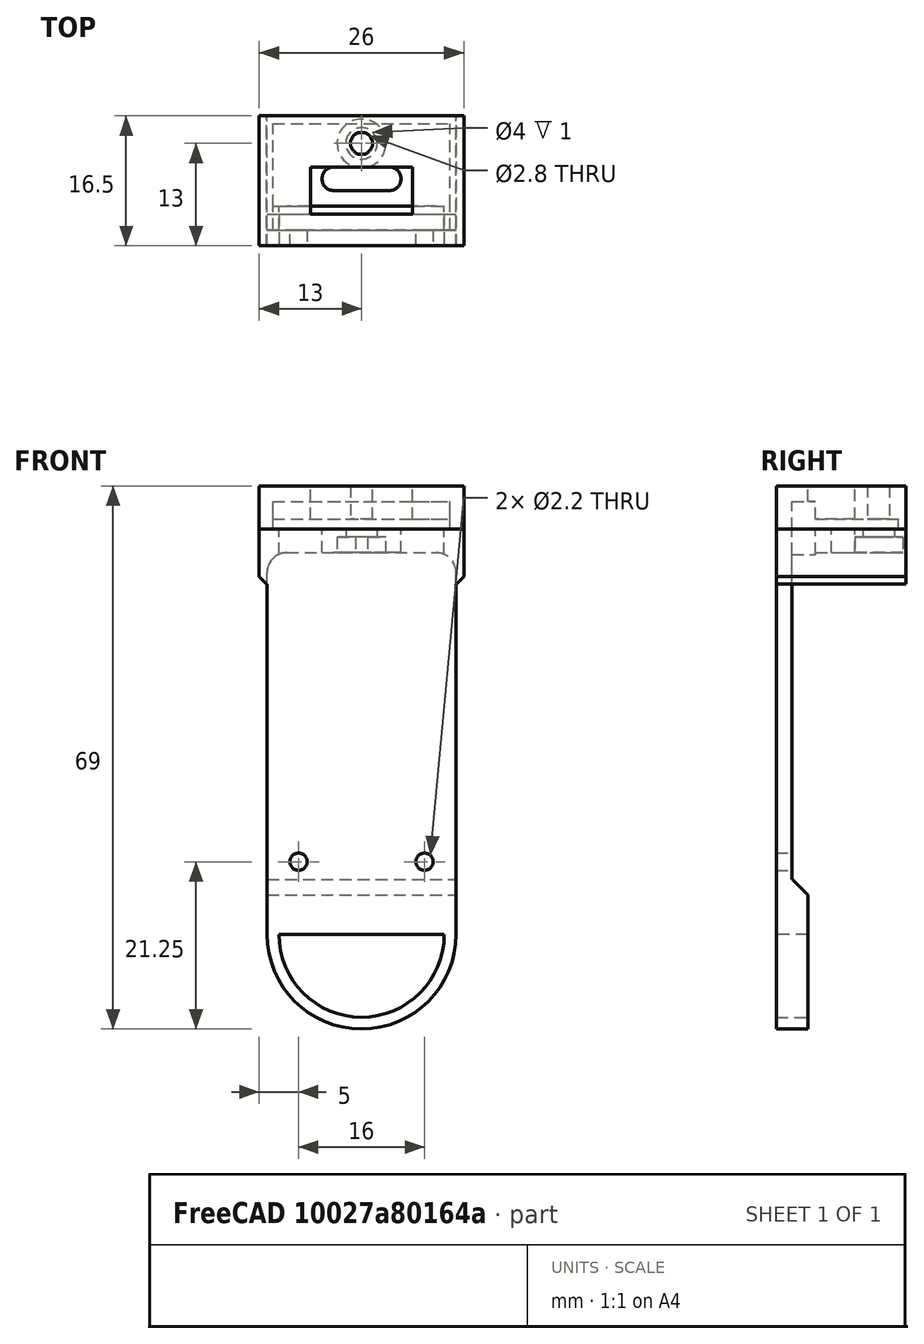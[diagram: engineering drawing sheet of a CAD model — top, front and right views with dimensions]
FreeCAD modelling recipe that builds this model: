
FCSTD DOCUMENT  (FreeCAD 1.0R39319 (Git))
Label: m5_stick_dht11
License: All rights reserved
LicenseURL: http://en.wikipedia.org/wiki/All_rights_reserved
objects: Part::Box×10, Part::Cylinder×7, Part::Cut×6, Part::MultiFuse×5, Part::Fillet×2, Part::Chamfer×2
note: 32 computed .brp shape members not serialized (recipe doc carries the construction recipe); baked Part::Feature solids carry a one-line shape summary decoded from their .brp

FEATURE [Part::Box] Box  label="Cube(inner_base)"
  AttacherType = Attacher::AttachEngine3D
  Height = 4
  Length = 24
  Width = 14.5
FEATURE [Part::Box] Box001  label="Cube(outer_base)"
  AttacherType = Attacher::AttachEngine3D
  Height = 7
  Length = 26
  Placement = pos=(-1,-2,0) rot=(0,0,1;0rad)
  Width = 16.5
FEATURE [Part::Fillet] Fillet
  Base = -> Box
  EdgeLinks = -> Box [Edge2,Edge6]
  Edges = 2 edges r=2.5: [Edge2,Edge6]
FEATURE [Part::Box] Box002  label="Cube(header_cutter)"
  AttacherType = Attacher::AttachEngine3D
  Height = 7
  Length = 21
  Placement = pos=(1.5,0,0) rot=(0,0,1;0rad)
  Width = 3
FEATURE [Part::Box] Box003  label="Cube(ir_reciever_header_cutter)"
  AttacherType = Attacher::AttachEngine3D
  Height = 7
  Length = 10
  Placement = pos=(7,5,0) rot=(0,0,1;0rad)
  Width = 3
FEATURE [Part::Fillet] Fillet001
  Base = -> Box003
  EdgeLinks = -> Box003 [Edge1,Edge3,Edge5,Edge7]
  Edges = 4 edges r=1.45: [Edge1,Edge3,Edge5,Edge7]
FEATURE [Part::Box] Box004  label="Cube(pcb_cut)"
  AttacherType = Attacher::AttachEngine3D
  Height = 3.5
  Length = 22.5
  Placement = pos=(0.75,0,7) rot=(0,0,1;0rad)
  Width = 3
FEATURE [Part::Box] Box005  label="Cube(top_cover)"
  AttacherType = Attacher::AttachEngine3D
  Height = 5.5
  Length = 26
  Placement = pos=(-1,-2,7) rot=(0,0,1;0rad)
  Width = 16.5
FEATURE [Part::Box] Box007  label="Cube(back_cover)"
  AttacherType = Attacher::AttachEngine3D
  Height = 43.5
  Length = 24
  Placement = pos=(0,-2,-37.5) rot=(0,0,1;0rad)
  Width = 2
FEATURE [Part::Cylinder] Cylinder001  label="Cylinder001(right_bolt_clear)"
  Angle = 360
  AttacherType = Attacher::AttachEngine3D
  FirstAngle = 0
  Height = 10
  Placement = pos=(4,0,-35.25) rot=(1,0,0;1.5708rad)
  Radius = 1.1
  SecondAngle = 0
FEATURE [Part::Cylinder] Cylinder002  label="Cylinder002(left_bolt_clear)"
  Angle = 360
  AttacherType = Attacher::AttachEngine3D
  FirstAngle = 0
  Height = 10
  Placement = pos=(20,0,-35.25) rot=(1,0,0;1.5708rad)
  Radius = 1.1
  SecondAngle = 0
FEATURE [Part::MultiFuse] Fusion004
  Shapes = -> [Cylinder002,Cylinder001]
FEATURE [Part::Cylinder] Cylinder005  label="Cylinder005(bolt_head)"
  Angle = 360
  AttacherType = Attacher::AttachEngine3D
  FirstAngle = 0
  Height = 2
  Placement = pos=(12,11,4) rot=(0,0,1;0rad)
  Radius = 3.1
  SecondAngle = 0
FEATURE [Part::Cut] Cut
  Base = -> Box001
  Tool = -> Fillet
FEATURE [Part::Cylinder] Cylinder006  label="Cylinder005(bolt_clear)"
  Angle = 360
  AttacherType = Attacher::AttachEngine3D
  FirstAngle = 0
  Height = 2
  Placement = pos=(12,11,5) rot=(0,0,1;0rad)
  Radius = 2
  SecondAngle = 0
FEATURE [Part::MultiFuse] Fusion
  Shapes = -> [Cylinder006,Cylinder005,Box002,Fillet001]
FEATURE [Part::Cut] Cut001
  Base = -> Cut
  Tool = -> Fusion
FEATURE [Part::Cylinder] Cylinder007  label="Cylinder005(bolt_thread)"
  Angle = 360
  AttacherType = Attacher::AttachEngine3D
  FirstAngle = 0
  Height = 6
  Placement = pos=(12,11,7) rot=(0,0,1;0rad)
  Radius = 1.4
  SecondAngle = 0
FEATURE [Part::Box] Box010  label="Cube(dht11)"
  AttacherType = Attacher::AttachEngine3D
  Height = 10
  Length = 13
  Placement = pos=(5.5,2,7) rot=(0,0,1;0rad)
  Width = 6
FEATURE [Part::MultiFuse] Fusion007
  Shapes = -> [Box010,Cylinder007,Box004]
FEATURE [Part::Cut] Cut003
  Base = -> Box005
  Tool = -> Fusion007
FEATURE [Part::Box] Box011  label="Cube(back_rest)"
  AttacherType = Attacher::AttachEngine3D
  Height = 7
  Length = 24
  Placement = pos=(0,-2,-44.5) rot=(0,0,1;0rad)
  Width = 4
FEATURE [Part::Cylinder] Cylinder008  label="Cylinder008(outer_hook)"
  Angle = 180
  AttacherType = Attacher::AttachEngine3D
  FirstAngle = 0
  Height = 4
  Placement = pos=(12,2,-44.5) rot=(0,0.707107,-0.707107;3.14159rad)
  Radius = 12
  SecondAngle = 0
FEATURE [Part::Cylinder] Cylinder009  label="Cylinder008(inner_hook)"
  Angle = 180
  AttacherType = Attacher::AttachEngine3D
  FirstAngle = 0
  Height = 4
  Placement = pos=(12,2,-44.5) rot=(0,0.707107,-0.707107;3.14159rad)
  Radius = 10.5
  SecondAngle = 0
FEATURE [Part::MultiFuse] Fusion008
  Shapes = -> [Box011,Cylinder008]
FEATURE [Part::Cut] Cut004
  Base = -> Fusion008
  Tool = -> Cylinder009
FEATURE [Part::Chamfer] Chamfer
  Base = -> Cut001
  EdgeLinks = -> Cut001 [Edge4,Edge36]
  Edges = 2 edges r=0.95: [Edge4,Edge36]
FEATURE [Part::Cut] Cut005
  Base = -> Box007
  Tool = -> Fusion004
FEATURE [Part::MultiFuse] Fusion009
  Shapes = -> [Cut005,Chamfer,Cut004]
FEATURE [Part::Chamfer] Chamfer001  label="Chamfer001(base)"
  Base = -> Fusion009
  EdgeLinks = -> Fusion009 [Edge57]
  Edges = 1 edges r=1.95: [Edge57]
FEATURE [Part::Box] Box012  label="Cube(pcb_cut)001"
  AttacherType = Attacher::AttachEngine3D
  Height = 1.25
  Length = 22.5
  Placement = pos=(0.75,3,7) rot=(0,0,1;0rad)
  Width = 10.5
FEATURE [Part::Cut] Cut006  label="Cut006(cover)"
  Base = -> Cut003
  Tool = -> Box012
